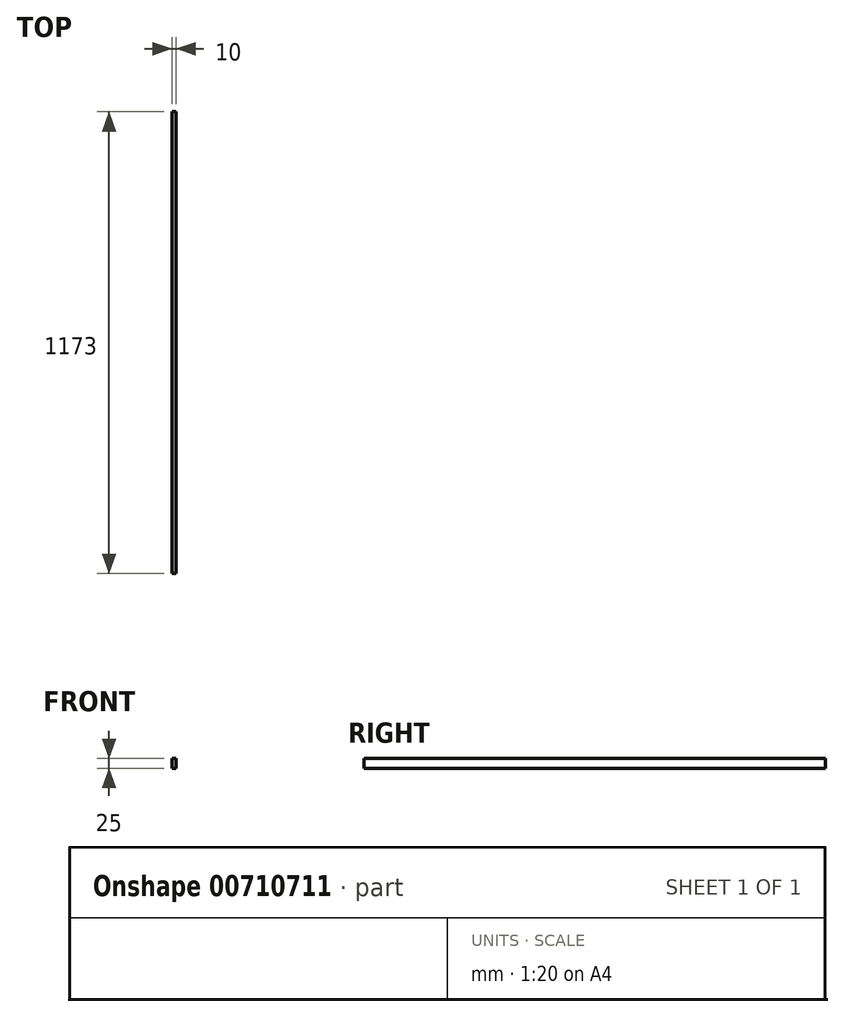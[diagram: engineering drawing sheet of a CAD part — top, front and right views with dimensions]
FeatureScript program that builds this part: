
annotation { "Feature Type Name" : "Feature", "Feature Type Description" : "" }
export const myFeature = defineFeature(function(context is Context, id is Id, definition is map)
    precondition{}
    {
        {
            assignVariable(context, id + "F0", {"name" : "l", "anyValue" : 1173});
        }
        {
            var Q0;
            Q0=qCreatedBy(makeId("Front.planeOp"),FACE);
            var sketch = newSketch(context, id + "F1", { "sketchPlane" : qUnion([Q0])});
            skLineSegment(sketch, "E0.bottom", {"start": v(0, 0) * mm, "end": v(10, 0) * mm});
            skLineSegment(sketch, "E0.top", {"start": v(0, 25) * mm, "end": v(10, 25) * mm});
            skLineSegment(sketch, "E0.left", {"start": v(0, 0) * mm, "end": v(0, 25) * mm});
            skLineSegment(sketch, "E0.right", {"start": v(10, 0) * mm, "end": v(10, 25) * mm});
            skSolve(sketch);
        }
        {
            var Q0;
            Q0=qSketchRegion(id+"F1",true);
            extrude(context, id + "F2", {"entities" : qUnion([Q0]), "depth" : (getVariable(context, 'l')) * mm, "offsetDistance" : 25 * mm});
        }
    });
